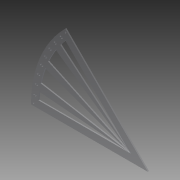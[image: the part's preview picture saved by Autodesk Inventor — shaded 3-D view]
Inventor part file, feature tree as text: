
AUTODESK INVENTOR PART (.ipt)
format: ipt  version: 2013 (Build 170138000, 138)  size: 171,520 bytes
history: native  units: in
note: dims shown in document units (in); Inventor stores cm internally (conversion verified against a paired STEP export)
features: extrude x4, sketch x4
ambient origin geometry x8: Origin, YZ Plane, XZ Plane, XY Plane, X Axis, Y Axis, Z Axis, Center Point
bodies: Solid1 (feature_tree)
feature tree (8):
  extrude  "Extrusion1"  Depth=0.375in
  extrude  "Extrusion2"  Depth=0.0625in
  extrude  "Extrusion4"  Depth=3.937in TaperAngle=45.0deg
  extrude  "Extrusion5"  Depth=0.125in
  sketch  "Sketch1"  dims[d0=0.125in d1=0.0in d2=0.375in]
  sketch  "Sketch4"  dims[d3=0.0625in d4=0.0625in]
  sketch  "Sketch7"  dims[d5=0.0625in d6=3.937in d8=45.0deg]
  sketch  "Sketch9"  dims[d10=0.25in d13=0.125in d14=0.25in d15=1.0in d16=0.0in d29=6.0in d31=0.125in d32=0.0in d34=0.75in d35=1.0in d36=1.0in d38=1.0in d39=1.0in d40=1.0in d41=1.0in d44=0.125in d45=0.0in]
